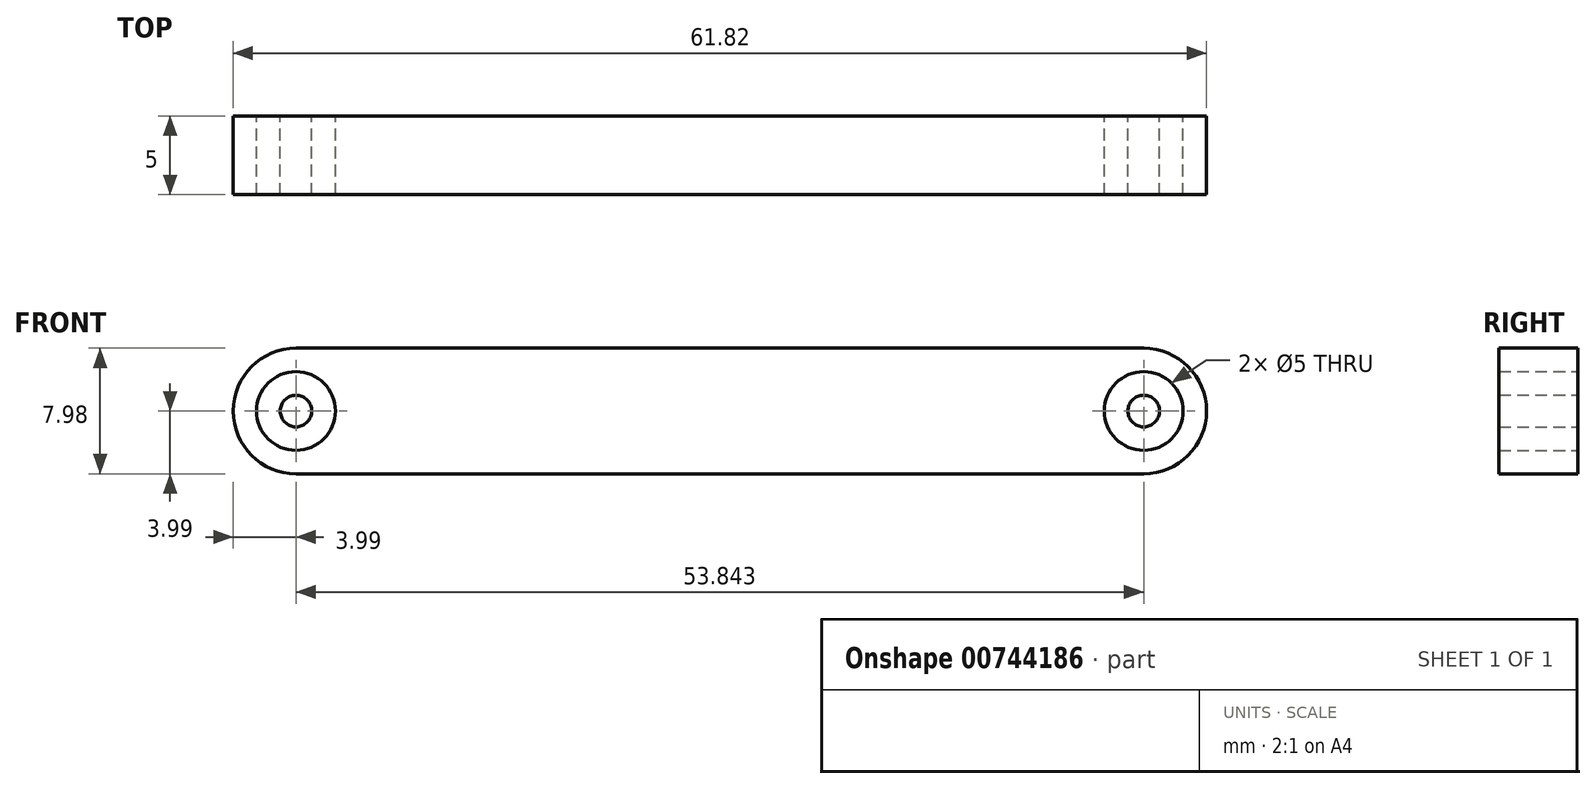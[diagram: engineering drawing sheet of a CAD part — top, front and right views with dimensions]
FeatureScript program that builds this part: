
annotation { "Feature Type Name" : "Feature", "Feature Type Description" : "" }
export const myFeature = defineFeature(function(context is Context, id is Id, definition is map)
    precondition{}
    {
        {
            var Q0;
            Q0=qCreatedBy(makeId("Front.planeOp"),FACE);
            var sketch = newSketch(context, id + "F0", { "sketchPlane" : qUnion([Q0])});
            skCircle(sketch, "E0", {"center": v(0, 0) * mm, "radius": 3.99 * mm});
            skCircle(sketch, "E1", {"center": v(53.84, 0) * mm, "radius": 3.99 * mm});
            skCircle(sketch, "E2", {"center": v(53.84, 0) * mm, "radius": 1 * mm});
            skCircle(sketch, "E3", {"center": v(0, 0) * mm, "radius": 1 * mm});
            skCircle(sketch, "E4", {"center": v(0, 0) * mm, "radius": 2.5 * mm});
            skCircle(sketch, "E5", {"center": v(53.84, 0) * mm, "radius": 2.5 * mm});
            skLineSegment(sketch, "E6", {"start": v(53.84, -3.99) * mm, "end": v(0, -3.99) * mm});
            skLineSegment(sketch, "E7", {"start": v(0, 3.99) * mm, "end": v(53.84, 3.99) * mm});
            skSolve(sketch);
        }
        {
            var Q0;
            Q0=qSketchRegion(id+"F0",true);
            var Q1;
            Q1=makeQuery(id+"F0.imprint","IMPRINT",FACE,{"disambiguationData":[TD([[makeQuery(id+"F0.imprint","IMPRINT",EDGE,{"derivedFrom":sQuery(id+"F0.wireOp",EDGE,"E0")}),1.0]])]});
            var Q2;
            Q2=makeQuery(id+"F0.imprint","IMPRINT",FACE,{"disambiguationData":[TD([[makeQuery(id+"F0.imprint","IMPRINT",EDGE,{"derivedFrom":sQuery(id+"F0.wireOp",EDGE,"E1")}),1.0]])]});
            var Q3;
            Q3=makeQuery(id+"F0.imprint","IMPRINT",FACE,{"disambiguationData":[TD([[makeQuery(id+"F0.imprint","IMPRINT",EDGE,{"derivedFrom":sQuery(id+"F0.wireOp",EDGE,"E3")}),1.0]])]});
            var Q4;
            Q4=makeQuery(id+"F0.imprint","IMPRINT",FACE,{"disambiguationData":[TD([[makeQuery(id+"F0.imprint","IMPRINT",EDGE,{"derivedFrom":sQuery(id+"F0.wireOp",EDGE,"E2")}),1.0]])]});
            extrude(context, id + "F1", {"entities" : qUnion([Q0, Q1, Q2, Q3, Q4]), "depth" : 5 * mm, "offsetDistance" : 25 * mm});
        }
    });
